# Revit family: 318_bf710bbbea7a439f93988170081b29
name_source: partatom
category: Pipe Accessories
units: mm (PartAtom-declared; Revit-internal decimal feet)

## family parameters
Always vertical = Yes
Cut with Voids When Loaded = No
Part Type = Valve - Normal
Round Connector Dimension = Use Diameter
Shared = No
Work Plane-Based = No

## types (1)
- FAR-3611 21
    BP = 25 mm
    CenSd_R_6 = 30 mm  [stored 0.0984252 ft]
    D1 = 50 mm  [stored 0.164042 ft]
    Description = 2" Brass modular manifold male-female, 2 port 1" female
    L = 210 mm  [stored 0.688976 ft]
    L1 = 22 mm
    L2 = 3 mm  [stored 0.00984252 ft]
    L3 = 185 mm
    L4 = 13 mm  [stored 0.0426509 ft]
    L5 = 105 mm  [stored 0.344488 ft]
    MP1 = 50 mm
    MP2 = 50 mm
    Manufacturer = FAR
    QmdConnectorList = 301;MP1;302;MP2;303;BP;304;BP
    R = 35 mm  [stored 0.114829 ft]
    R1 = 25 mm  [stored 0.082021 ft]
    R3 = 30 mm  [stored 0.0984252 ft]
    R6 = 14 mm  [stored 0.0459318 ft]
    R8 = 25 mm  [stored 0.082021 ft]
    URL = www.far.eu
    Z = 47 mm  [stored 0.154199 ft]
    Z__ve = -47 mm  [stored -0.154199 ft]
    magiPartTypeId = 318
    magiProductCode = FAR-3611 21
    magiProductFamilyId = bf710bbbea7a439f93988170081b29
    magiProductId = bf710bbbea7a439f93988170081b29

note: [stored X ft] marks values corroborated as IEEE doubles in the binary element streams (Revit-internal decimal feet)

## geometry (parser evidence)
native form markers: Sweep x2
no freeform markers — native parametric forms only
